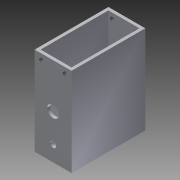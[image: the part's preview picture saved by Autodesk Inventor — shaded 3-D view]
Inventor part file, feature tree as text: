
AUTODESK INVENTOR PART (.ipt)
format: ipt  version: 2013 (Build 170138000, 138)  size: 161,280 bytes
history: native  units: mm
features: sketch x6, hole x4, thread x4, extrude x2, other x1
ambient origin geometry x1: Origin
feature tree (17):
  other  "ソリッド1"
  extrude  "押し出し1"  Depth=25.0mm
  extrude  "押し出し2"  Depth=50.0mm
  hole  "穴1"  [1 undecoded]
  hole  "穴2"  [1 undecoded]
  hole  "穴4"  [1 undecoded]
  thread  "ねじ1"
  thread  "ねじ2"
  thread  "ねじ3"
  thread  "ねじ4"
  hole  "穴5"  [1 undecoded]
  sketch  "スケッチ1"
  sketch  "スケッチ2"
  sketch  "スケッチ3"
  sketch  "スケッチ4"
  sketch  "スケッチ5"
  sketch  "スケッチ7"
note: 4 required parameter values undecoded (feature->parameter linkage not recoverable at this tier; creation-order binding heuristic only, values carry confidence <= 0.55)
